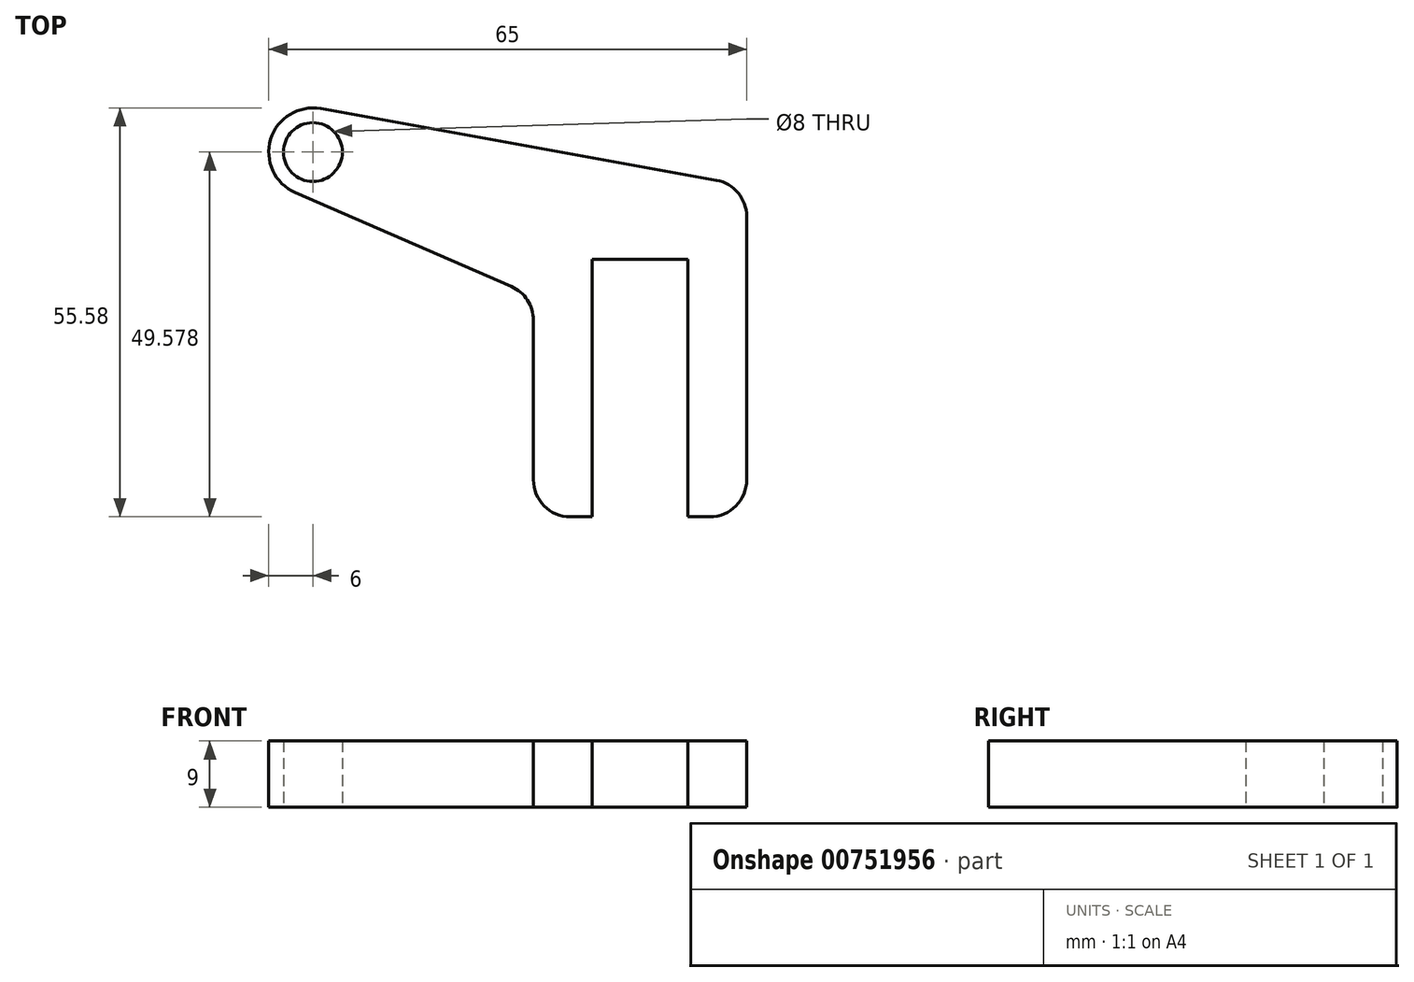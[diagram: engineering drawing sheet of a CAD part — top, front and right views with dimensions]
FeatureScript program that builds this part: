
annotation { "Feature Type Name" : "Feature", "Feature Type Description" : "" }
export const myFeature = defineFeature(function(context is Context, id is Id, definition is map)
    precondition{}
    {
        {
            var Q0;
            Q0=qCreatedBy(makeId("Top.planeOp"),FACE);
            var sketch = newSketch(context, id + "F0", { "sketchPlane" : qUnion([Q0])});
            skLineSegment(sketch, "E0", {"start": v(0, 0) * mm, "end": v(0, 35) * mm});
            skLineSegment(sketch, "E1", {"start": v(0, 35) * mm, "end": v(13, 35) * mm});
            skLineSegment(sketch, "E2", {"start": v(13, 35) * mm, "end": v(13, 0) * mm});
            skLineSegment(sketch, "E3", {"start": v(13, 0) * mm, "end": v(21, 0) * mm});
            skLineSegment(sketch, "E4", {"start": v(21, 0) * mm, "end": v(21, 45) * mm});
            skLineSegment(sketch, "E5", {"start": v(21, 45) * mm, "end": v(-8, 45) * mm});
            skLineSegment(sketch, "E6", {"start": v(-8, 45) * mm, "end": v(-8, 0) * mm});
            skLineSegment(sketch, "E7", {"start": v(-8, 0) * mm, "end": v(0, 0) * mm});
            skCircle(sketch, "E8", {"center": v(-38, 35.58) * mm, "radius": 20 * mm, "construction": true});
            skCircle(sketch, "E9", {"center": v(-38, 49.58) * mm, "radius": 6 * mm});
            skLineSegment(sketch, "E10", {"start": v(-40.4, 44.07) * mm, "end": v(-8, 30) * mm});
            skLineSegment(sketch, "E11", {"start": v(21, 45) * mm, "end": v(-36.93, 55.48) * mm});
            skCircle(sketch, "E12", {"center": v(-38, 49.58) * mm, "radius": 4 * mm});
            skSolve(sketch);
        }
        {
            var Q0;
            {var subQ2=sQuery(id+"F0.wireOp",EDGE,"E5");Q0=makeQuery(id+"F0.imprint","IMPRINT",FACE,{"disambiguationData":[TD([[makeQuery(id+"F0.imprint","IMPRINT",EDGE,{"derivedFrom":subQ2}),-1.0]])]});}
            var Q1;
            Q1=makeQuery(id+"F0.imprint","IMPRINT",FACE,{"disambiguationData":[TD([[makeQuery(id+"F0.imprint","IMPRINT",EDGE,{"derivedFrom":sQuery(id+"F0.wireOp",EDGE,"E12")}),-1.0]])]});
            var Q2;
            Q2=makeQuery(id+"F0.imprint","IMPRINT",FACE,{"disambiguationData":[TD([[makeQuery(id+"F0.imprint","IMPRINT",EDGE,{"derivedFrom":sQuery(id+"F0.wireOp",EDGE,"E0")}),1.0]])]});
            extrude(context, id + "F1", {"entities" : qUnion([Q0, Q1, Q2]), "depth" : 9 * mm, "offsetDistance" : 25 * mm});
        }
        {
            var Q0;
            Q0=makeQuery(id+"F1.opExtrude","SWEPT_EDGE",EDGE,{"disambiguationData":[OSD([sQuery(id+"F0.wireOp",EDGE,"E6"),sQuery(id+"F0.wireOp",EDGE,"E10")])]});
            var Q1;
            Q1=makeQuery(id+"F1.opExtrude","SWEPT_EDGE",EDGE,{"disambiguationData":[OSD([sQuery(id+"F0.wireOp",EDGE,"E4"),sQuery(id+"F0.wireOp",EDGE,"E5"),sQuery(id+"F0.wireOp",EDGE,"E11")])]});
            var Q2;
            Q2=makeQuery(id+"F1.opExtrude","SWEPT_EDGE",EDGE,{"disambiguationData":[OSD([sQuery(id+"F0.wireOp",EDGE,"E6"),sQuery(id+"F0.wireOp",EDGE,"E7")])]});
            var Q3;
            Q3=makeQuery(id+"F1.opExtrude","SWEPT_EDGE",EDGE,{"disambiguationData":[OSD([sQuery(id+"F0.wireOp",EDGE,"E3"),sQuery(id+"F0.wireOp",EDGE,"E4")])]});
            fillet(context, id + "F2", {"entities" : qUnion([Q0, Q1, Q2, Q3]), "radius" : 5 * mm, "tangentPropagation" : true, "allowEdgeOverflow" : false});
        }
    });
